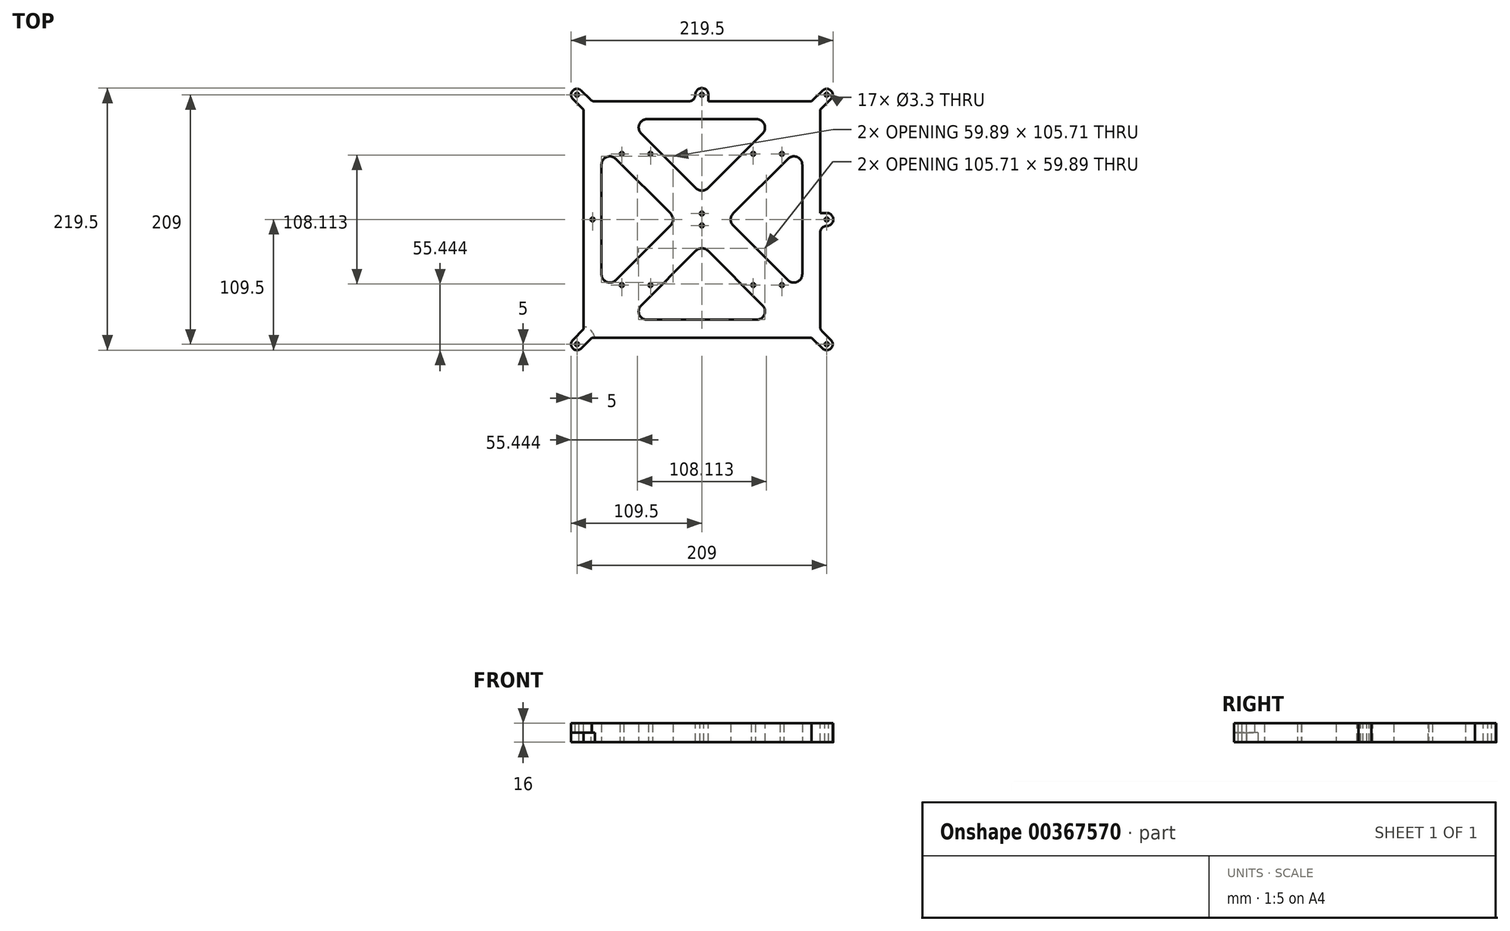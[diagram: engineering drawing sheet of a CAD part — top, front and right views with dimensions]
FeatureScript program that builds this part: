
annotation { "Feature Type Name" : "Feature", "Feature Type Description" : "" }
export const myFeature = defineFeature(function(context is Context, id is Id, definition is map)
    precondition{}
    {
        {
            var Q0;
            Q0=qCreatedBy(makeId("Top.planeOp"),FACE);
            var sketch = newSketch(context, id + "F0", { "sketchPlane" : qUnion([Q0])});
            skLineSegment(sketch, "E0.bottom", {"start": v(99, 99) * mm, "end": v(-99, 99) * mm});
            skLineSegment(sketch, "E0.top", {"start": v(99, -99) * mm, "end": v(-99, -99) * mm});
            skLineSegment(sketch, "E0.left", {"start": v(99, 99) * mm, "end": v(99, -99) * mm});
            skLineSegment(sketch, "E0.right", {"start": v(-99, 99) * mm, "end": v(-99, -99) * mm});
            skPoint(sketch, "E0.middle", {"position": v(0, 0) * mm});
            skLineSegment(sketch, "E1", {"start": v(99, 99) * mm, "end": v(-99, -99) * mm, "construction": true});
            skLineSegment(sketch, "E2", {"start": v(0, 21.21) * mm, "end": v(62.79, 84) * mm});
            skLineSegment(sketch, "E3.MirrorCS", {"start": v(0, 21.21) * mm, "end": v(-62.79, 84) * mm});
            skLineSegment(sketch, "E4", {"start": v(62.79, 84) * mm, "end": v(-62.79, 84) * mm});
            skLineSegment(sketch, "E5", {"start": v(-99, 99) * mm, "end": v(99, -99) * mm, "construction": true});
            skLineSegment(sketch, "E6.MirrorCS", {"start": v(-21.21, 0) * mm, "end": v(-84, 62.79) * mm});
            skLineSegment(sketch, "E7.MirrorCS", {"start": v(-84, -62.79) * mm, "end": v(-84, 62.79) * mm});
            skLineSegment(sketch, "E8.MirrorCS", {"start": v(-21.21, 0) * mm, "end": v(-84, -62.79) * mm});
            skLineSegment(sketch, "E9.MirrorCS", {"start": v(21.21, 0) * mm, "end": v(84, 62.79) * mm});
            skLineSegment(sketch, "E10.MirrorCS", {"start": v(84, 62.79) * mm, "end": v(84, -62.79) * mm});
            skLineSegment(sketch, "E11.MirrorCS", {"start": v(21.21, 0) * mm, "end": v(84, -62.79) * mm});
            skLineSegment(sketch, "E12.MirrorCS", {"start": v(0, -21.21) * mm, "end": v(-62.79, -84) * mm});
            skLineSegment(sketch, "E13.MirrorCS", {"start": v(0, -21.21) * mm, "end": v(62.79, -84) * mm});
            skLineSegment(sketch, "E14.MirrorCS", {"start": v(-62.79, -84) * mm, "end": v(62.79, -84) * mm});
            skLineSegment(sketch, "E15", {"start": v(-55, 55) * mm, "end": v(-43, 55) * mm, "construction": true});
            skLineSegment(sketch, "E16", {"start": v(-55, 55) * mm, "end": v(-67, 55) * mm, "construction": true});
            skLineSegment(sketch, "E17.MirrorCS", {"start": v(55, 55) * mm, "end": v(67, 55) * mm, "construction": true});
            skLineSegment(sketch, "E18.MirrorCS", {"start": v(55, 55) * mm, "end": v(43, 55) * mm, "construction": true});
            skLineSegment(sketch, "E19.MirrorCS", {"start": v(55, -55) * mm, "end": v(67, -55) * mm, "construction": true});
            skLineSegment(sketch, "E20.MirrorCS", {"start": v(-55, -55) * mm, "end": v(-43, -55) * mm, "construction": true});
            skLineSegment(sketch, "E21.MirrorCS", {"start": v(-55, -55) * mm, "end": v(-67, -55) * mm, "construction": true});
            skLineSegment(sketch, "E22.MirrorCS", {"start": v(55, -55) * mm, "end": v(43, -55) * mm, "construction": true});
            skSolve(sketch);
        }
        {
            var Q0;
            Q0=makeQuery(id+"F0.imprint","IMPRINT",FACE,{"disambiguationData":[TD([[makeQuery(id+"F0.imprint","IMPRINT",EDGE,{"derivedFrom":sQuery(id+"F0.wireOp",EDGE,"E0.bottom")}),1.0]])]});
            extrude(context, id + "F1", {"entities" : qUnion([Q0]), "depth" : 16 * mm});
        }
        {
            var Q0;
            Q0=makeQuery(id+"F1.opExtrude","CAP_FACE",FACE,{"disambiguationData":[OSD([sQuery(id+"F0.wireOp",EDGE,"E0.bottom"),sQuery(id+"F0.wireOp",EDGE,"E0.top"),sQuery(id+"F0.wireOp",EDGE,"E0.left"),sQuery(id+"F0.wireOp",EDGE,"E0.right"),sQuery(id+"F0.wireOp",EDGE,"E2"),sQuery(id+"F0.wireOp",EDGE,"E3.MirrorCS"),sQuery(id+"F0.wireOp",EDGE,"E4"),sQuery(id+"F0.wireOp",EDGE,"E6.MirrorCS"),sQuery(id+"F0.wireOp",EDGE,"E7.MirrorCS"),sQuery(id+"F0.wireOp",EDGE,"E8.MirrorCS"),sQuery(id+"F0.wireOp",EDGE,"E9.MirrorCS"),sQuery(id+"F0.wireOp",EDGE,"E10.MirrorCS"),sQuery(id+"F0.wireOp",EDGE,"E11.MirrorCS"),sQuery(id+"F0.wireOp",EDGE,"E12.MirrorCS"),sQuery(id+"F0.wireOp",EDGE,"E13.MirrorCS"),sQuery(id+"F0.wireOp",EDGE,"E14.MirrorCS")])],"isStart":false});
            var sketch = newSketch(context, id + "F2", { "sketchPlane" : qUnion([Q0])});
            skLineSegment(sketch, "E23", {"start": v(-99, 99) * mm, "end": v(-104.5, 104.5) * mm, "construction": true});
            skLineSegment(sketch, "E24.0", {"start": v(-91.93, 99) * mm, "end": v(-100.96, 108.04) * mm});
            skLineSegment(sketch, "E25.0", {"start": v(-99, 91.93) * mm, "end": v(-108.04, 100.96) * mm});
            skArc(sketch, "E26", {"start": v(-108.04, 100.96) * mm, "mid": v(-108.04, 108.04) * mm, "end": v(-100.96, 108.04) * mm});
            skLineSegment(sketch, "E27.MirrorCS", {"start": v(99, 91.93) * mm, "end": v(108.04, 100.96) * mm});
            skLineSegment(sketch, "E28.MirrorCS", {"start": v(99, 99) * mm, "end": v(104.5, 104.5) * mm, "construction": true});
            skLineSegment(sketch, "E29.MirrorCS", {"start": v(91.93, 99) * mm, "end": v(100.96, 108.04) * mm});
            skArc(sketch, "E30.MirrorCS", {"start": v(108.04, 100.96) * mm, "mid": v(108.04, 108.04) * mm, "end": v(100.96, 108.04) * mm});
            skLineSegment(sketch, "E31.MirrorCS", {"start": v(99, -99) * mm, "end": v(104.5, -104.5) * mm, "construction": true});
            skLineSegment(sketch, "E32.MirrorCS", {"start": v(-99, -99) * mm, "end": v(-104.5, -104.5) * mm, "construction": true});
            skLineSegment(sketch, "E33.MirrorCS", {"start": v(-99, -91.93) * mm, "end": v(-108.04, -100.96) * mm});
            skLineSegment(sketch, "E34.MirrorCS", {"start": v(91.93, -99) * mm, "end": v(100.96, -108.04) * mm});
            skArc(sketch, "E35.MirrorCS", {"start": v(108.04, -100.96) * mm, "mid": v(108.04, -108.04) * mm, "end": v(100.96, -108.04) * mm});
            skLineSegment(sketch, "E36.MirrorCS", {"start": v(99, -91.93) * mm, "end": v(108.04, -100.96) * mm});
            skArc(sketch, "E37.MirrorCS", {"start": v(-108.04, -100.96) * mm, "mid": v(-108.04, -108.04) * mm, "end": v(-100.96, -108.04) * mm});
            skLineSegment(sketch, "E38.MirrorCS", {"start": v(-91.93, -99) * mm, "end": v(-100.96, -108.04) * mm});
            skLineSegment(sketch, "E39", {"start": v(-5.5, 99) * mm, "end": v(-5.5, 110) * mm});
            skLineSegment(sketch, "E40", {"start": v(-5.5, 110) * mm, "end": v(5.5, 110) * mm});
            skLineSegment(sketch, "E41", {"start": v(5.5, 110) * mm, "end": v(5.5, 99) * mm});
            skLineSegment(sketch, "E42", {"start": v(99, 5.5) * mm, "end": v(110, 5.5) * mm});
            skLineSegment(sketch, "E43", {"start": v(110, 5.5) * mm, "end": v(110, -5.5) * mm});
            skLineSegment(sketch, "E44", {"start": v(110, -5.5) * mm, "end": v(99, -5.5) * mm});
            skLineSegment(sketch, "E45", {"start": v(110, 0) * mm, "end": v(99, 0) * mm, "construction": true});
            skLineSegment(sketch, "E46", {"start": v(0, 110) * mm, "end": v(0, 99) * mm, "construction": true});
            skLineSegment(sketch, "E47", {"start": v(0, 104.5) * mm, "end": v(5.5, 110) * mm, "construction": true});
            skLineSegment(sketch, "E48", {"start": v(104.5, 0) * mm, "end": v(110, -5.5) * mm, "construction": true});
            skLineSegment(sketch, "E49", {"start": v(0, 0) * mm, "end": v(0, -5) * mm, "construction": true});
            skLineSegment(sketch, "E50", {"start": v(0, 0) * mm, "end": v(0, 5) * mm, "construction": true});
            skSolve(sketch);
        }
        {
            var Q0;
            {var subQ4=sQuery(id+"F2.wireOp",EDGE,"E33.MirrorCS");Q0=makeQuery(id+"F2.imprint","IMPRINT",FACE,{"disambiguationData":[TD([[makeQuery(id+"F2.imprint","IMPRINT",EDGE,{"derivedFrom":subQ4}),1.0]])]});}
            var Q1;
            {var subQ3=sQuery(id+"F2.wireOp",EDGE,"E34.MirrorCS");Q1=makeQuery(id+"F2.imprint","IMPRINT",FACE,{"disambiguationData":[TD([[makeQuery(id+"F2.imprint","IMPRINT",EDGE,{"derivedFrom":subQ3}),1.0]])]});}
            var Q2;
            {var subQ0=sQuery(id+"F2.wireOp",EDGE,"E42");Q2=makeQuery(id+"F2.imprint","IMPRINT",FACE,{"disambiguationData":[TD([[makeQuery(id+"F2.imprint","IMPRINT",EDGE,{"derivedFrom":subQ0}),-1.0]])]});}
            var Q3;
            {var subQ4=sQuery(id+"F2.wireOp",EDGE,"E27.MirrorCS");Q3=makeQuery(id+"F2.imprint","IMPRINT",FACE,{"disambiguationData":[TD([[makeQuery(id+"F2.imprint","IMPRINT",EDGE,{"derivedFrom":subQ4}),1.0]])]});}
            var Q4;
            {var subQ3=sQuery(id+"F2.wireOp",EDGE,"E24.0");Q4=makeQuery(id+"F2.imprint","IMPRINT",FACE,{"disambiguationData":[TD([[makeQuery(id+"F2.imprint","IMPRINT",EDGE,{"derivedFrom":subQ3}),1.0]])]});}
            var Q5;
            {var subQ0=sQuery(id+"F2.wireOp",EDGE,"E39");Q5=makeQuery(id+"F2.imprint","IMPRINT",FACE,{"disambiguationData":[TD([[makeQuery(id+"F2.imprint","IMPRINT",EDGE,{"derivedFrom":subQ0}),-1.0]])]});}
            var Q6;
            Q6=makeQuery(id+"F1.opExtrude","CAP_FACE",FACE,{"disambiguationData":[OSD([sQuery(id+"F0.wireOp",EDGE,"E0.bottom"),sQuery(id+"F0.wireOp",EDGE,"E0.top"),sQuery(id+"F0.wireOp",EDGE,"E0.left"),sQuery(id+"F0.wireOp",EDGE,"E0.right"),sQuery(id+"F0.wireOp",EDGE,"E2"),sQuery(id+"F0.wireOp",EDGE,"E3.MirrorCS"),sQuery(id+"F0.wireOp",EDGE,"E4"),sQuery(id+"F0.wireOp",EDGE,"E6.MirrorCS"),sQuery(id+"F0.wireOp",EDGE,"E7.MirrorCS"),sQuery(id+"F0.wireOp",EDGE,"E8.MirrorCS"),sQuery(id+"F0.wireOp",EDGE,"E9.MirrorCS"),sQuery(id+"F0.wireOp",EDGE,"E10.MirrorCS"),sQuery(id+"F0.wireOp",EDGE,"E11.MirrorCS"),sQuery(id+"F0.wireOp",EDGE,"E12.MirrorCS"),sQuery(id+"F0.wireOp",EDGE,"E13.MirrorCS"),sQuery(id+"F0.wireOp",EDGE,"E14.MirrorCS")])],"isStart":true});
            extrude(context, id + "F3", {"entities" : qUnion([Q0, Q1, Q2, Q3, Q4, Q5]), "operationType" : NewBodyOperationType.ADD, "endBound" : BoundingType.UP_TO_SURFACE, "oppositeDirection" : true, "endBoundEntityFace" : qUnion([Q6]), "depth" : 25 * mm});
        }
        {
            var Q0;
            {var subQ0=sQuery(id+"F0.wireOp",EDGE,"E0.left");var subQ1=sQuery(id+"F0.wireOp",EDGE,"E14.MirrorCS");var subQ2=sQuery(id+"F0.wireOp",EDGE,"E13.MirrorCS");var subQ3=sQuery(id+"F0.wireOp",EDGE,"E12.MirrorCS");var subQ4=sQuery(id+"F0.wireOp",EDGE,"E11.MirrorCS");var subQ5=sQuery(id+"F0.wireOp",EDGE,"E10.MirrorCS");var subQ6=sQuery(id+"F0.wireOp",EDGE,"E9.MirrorCS");var subQ7=sQuery(id+"F0.wireOp",EDGE,"E8.MirrorCS");var subQ8=sQuery(id+"F0.wireOp",EDGE,"E7.MirrorCS");var subQ9=sQuery(id+"F0.wireOp",EDGE,"E6.MirrorCS");var subQ10=sQuery(id+"F0.wireOp",EDGE,"E4");var subQ11=sQuery(id+"F0.wireOp",EDGE,"E3.MirrorCS");var subQ12=sQuery(id+"F0.wireOp",EDGE,"E2");var subQ13=sQuery(id+"F0.wireOp",EDGE,"E0.right");var subQ14=sQuery(id+"F0.wireOp",EDGE,"E0.top");var subQ15=sQuery(id+"F0.wireOp",EDGE,"E0.bottom");Q0=makeQuery(id+"F3.boolean.opBoolean","MERGE",FACE,{"derivedFrom":[makeQuery(id+"F1.opExtrude","CAP_FACE",FACE,{"disambiguationData":[OSD([subQ15,subQ14,subQ0,subQ13,subQ12,subQ11,subQ10,subQ9,subQ8,subQ7,subQ6,subQ5,subQ4,subQ3,subQ2,subQ1])],"isStart":true}),makeQuery(id+"F3.opExtrude","CAP_FACE",FACE,{"disambiguationData":[OSD([subQ15,subQ14,subQ0,subQ13,subQ12,subQ11,subQ10,subQ9,subQ8,subQ7,subQ6,subQ5,subQ4,subQ3,subQ2,subQ1]),ownerDisambiguation([makeQuery(id+"F3.opExtrude","SWEPT_BODY",BODY,{"disambiguationData":[OSD([subQ15,subQ13,sQuery(id+"F2.wireOp",EDGE,"E24.0"),sQuery(id+"F2.wireOp",EDGE,"E25.0"),sQuery(id+"F2.wireOp",EDGE,"E26")])]})])],"isStart":false}),makeQuery(id+"F3.opExtrude","CAP_FACE",FACE,{"disambiguationData":[OSD([subQ15,subQ14,subQ0,subQ13,subQ12,subQ11,subQ10,subQ9,subQ8,subQ7,subQ6,subQ5,subQ4,subQ3,subQ2,subQ1]),ownerDisambiguation([makeQuery(id+"F3.opExtrude","SWEPT_BODY",BODY,{"disambiguationData":[OSD([subQ15,subQ0,sQuery(id+"F2.wireOp",EDGE,"E27.MirrorCS"),sQuery(id+"F2.wireOp",EDGE,"E29.MirrorCS"),sQuery(id+"F2.wireOp",EDGE,"E30.MirrorCS")])]})])],"isStart":false}),makeQuery(id+"F3.opExtrude","CAP_FACE",FACE,{"disambiguationData":[OSD([subQ15,subQ14,subQ0,subQ13,subQ12,subQ11,subQ10,subQ9,subQ8,subQ7,subQ6,subQ5,subQ4,subQ3,subQ2,subQ1]),ownerDisambiguation([makeQuery(id+"F3.opExtrude","SWEPT_BODY",BODY,{"disambiguationData":[OSD([subQ14,subQ13,sQuery(id+"F2.wireOp",EDGE,"E33.MirrorCS"),sQuery(id+"F2.wireOp",EDGE,"E37.MirrorCS"),sQuery(id+"F2.wireOp",EDGE,"E38.MirrorCS")])]})])],"isStart":false}),makeQuery(id+"F3.opExtrude","CAP_FACE",FACE,{"disambiguationData":[OSD([subQ15,subQ14,subQ0,subQ13,subQ12,subQ11,subQ10,subQ9,subQ8,subQ7,subQ6,subQ5,subQ4,subQ3,subQ2,subQ1]),ownerDisambiguation([makeQuery(id+"F3.opExtrude","SWEPT_BODY",BODY,{"disambiguationData":[OSD([subQ14,subQ0,sQuery(id+"F2.wireOp",EDGE,"E34.MirrorCS"),sQuery(id+"F2.wireOp",EDGE,"E35.MirrorCS"),sQuery(id+"F2.wireOp",EDGE,"E36.MirrorCS")])]})])],"isStart":false}),makeQuery(id+"F3.opExtrude","CAP_FACE",FACE,{"disambiguationData":[OSD([subQ15,subQ14,subQ0,subQ13,subQ12,subQ11,subQ10,subQ9,subQ8,subQ7,subQ6,subQ5,subQ4,subQ3,subQ2,subQ1]),ownerDisambiguation([makeQuery(id+"F3.opExtrude","SWEPT_BODY",BODY,{"disambiguationData":[OSD([subQ15,sQuery(id+"F2.wireOp",EDGE,"E39"),sQuery(id+"F2.wireOp",EDGE,"E40"),sQuery(id+"F2.wireOp",EDGE,"E41")])]})])],"isStart":false}),makeQuery(id+"F3.opExtrude","CAP_FACE",FACE,{"disambiguationData":[OSD([subQ15,subQ14,subQ0,subQ13,subQ12,subQ11,subQ10,subQ9,subQ8,subQ7,subQ6,subQ5,subQ4,subQ3,subQ2,subQ1]),ownerDisambiguation([makeQuery(id+"F3.opExtrude","SWEPT_BODY",BODY,{"disambiguationData":[OSD([subQ0,sQuery(id+"F2.wireOp",EDGE,"E42"),sQuery(id+"F2.wireOp",EDGE,"E43"),sQuery(id+"F2.wireOp",EDGE,"E44")])]})])],"isStart":false})]});}
            var sketch = newSketch(context, id + "F4", { "sketchPlane" : qUnion([Q0])});
            skPoint(sketch, "E51.0", {"position": v(-101.75, -101.75) * mm});
            skPoint(sketch, "E52.0", {"position": v(0, -104.5) * mm});
            skPoint(sketch, "E53.0", {"position": v(101.75, -101.75) * mm});
            skPoint(sketch, "E54.0", {"position": v(104.5, 0) * mm});
            skPoint(sketch, "E55.0", {"position": v(101.75, 101.75) * mm});
            skPoint(sketch, "E56.0", {"position": v(-101.75, 101.75) * mm});
            skCircle(sketch, "E57", {"center": v(-101.75, 101.75) * mm, "radius": 12.5 * mm});
            skCircle(sketch, "E58", {"center": v(101.75, 101.75) * mm, "radius": 12.5 * mm});
            skCircle(sketch, "E59", {"center": v(-101.75, -101.75) * mm, "radius": 12.5 * mm});
            skCircle(sketch, "E60", {"center": v(101.75, -101.75) * mm, "radius": 12.5 * mm});
            skCircle(sketch, "E61", {"center": v(0, -104.5) * mm, "radius": 10 * mm});
            skCircle(sketch, "E62", {"center": v(104.5, 0) * mm, "radius": 10 * mm});
            skLineSegment(sketch, "E63", {"start": v(-99, 0) * mm, "end": v(-84, 0) * mm});
            skCircle(sketch, "E64", {"center": v(-91.5, 0) * mm, "radius": 2.5 * mm});
            skSolve(sketch);
        }
        {
            var Q0;
            {var subQ1=sQuery(id+"F0.wireOp",EDGE,"E0.top");var subQ6=sQuery(id+"F4.wireOp",EDGE,"E57");var subQ8=makeQuery(id+"F1.opExtrude","CAP_EDGE",EDGE,{"disambiguationData":[OSD([subQ1])],"isStart":true});var subQ9=makeQuery(id+"F4.imprint","INTERSECT",VERTEX,{"derivedFrom":[subQ8,subQ6]});Q0=makeQuery(id+"F4.imprint","IMPRINT",FACE,{"disambiguationData":[TD([[makeQuery(id+"F4.imprint","IMPRINT",EDGE,{"disambiguationData":[TD([[subQ9,1.0]])],"derivedFrom":subQ6}),1.0]])]});}
            var Q1;
            {var subQ1=sQuery(id+"F0.wireOp",EDGE,"E14.MirrorCS");var subQ2=sQuery(id+"F0.wireOp",EDGE,"E13.MirrorCS");var subQ3=sQuery(id+"F0.wireOp",EDGE,"E12.MirrorCS");var subQ4=sQuery(id+"F0.wireOp",EDGE,"E11.MirrorCS");var subQ5=sQuery(id+"F0.wireOp",EDGE,"E10.MirrorCS");var subQ6=sQuery(id+"F0.wireOp",EDGE,"E9.MirrorCS");var subQ7=sQuery(id+"F0.wireOp",EDGE,"E8.MirrorCS");var subQ8=sQuery(id+"F0.wireOp",EDGE,"E7.MirrorCS");var subQ9=sQuery(id+"F0.wireOp",EDGE,"E6.MirrorCS");var subQ10=sQuery(id+"F0.wireOp",EDGE,"E4");var subQ11=sQuery(id+"F0.wireOp",EDGE,"E3.MirrorCS");var subQ12=sQuery(id+"F0.wireOp",EDGE,"E2");var subQ13=sQuery(id+"F0.wireOp",EDGE,"E0.right");var subQ14=sQuery(id+"F0.wireOp",EDGE,"E0.left");var subQ15=sQuery(id+"F0.wireOp",EDGE,"E0.top");var subQ16=sQuery(id+"F0.wireOp",EDGE,"E0.bottom");var subQ17=makeQuery(id+"F1.opExtrude","CAP_FACE",FACE,{"disambiguationData":[OSD([subQ16,subQ15,subQ14,subQ13,subQ12,subQ11,subQ10,subQ9,subQ8,subQ7,subQ6,subQ5,subQ4,subQ3,subQ2,subQ1])],"isStart":true});var subQ22=sQuery(id+"F2.wireOp",EDGE,"E24.0");var subQ26=makeQuery(id+"F3.opExtrude","TWEAK_EDGE",EDGE,{"derivedFrom":[subQ17,makeQuery(id+"F2.imprint","IMPRINT",EDGE,{"derivedFrom":subQ22})]});Q1=makeQuery(id+"F4.imprint","IMPRINT",FACE,{"disambiguationData":[TD([[makeQuery(id+"F4.imprint","IMPRINT",EDGE,{"derivedFrom":subQ26}),1.0]])]});}
            var Q2;
            {var subQ1=sQuery(id+"F0.wireOp",EDGE,"E14.MirrorCS");var subQ2=sQuery(id+"F0.wireOp",EDGE,"E13.MirrorCS");var subQ3=sQuery(id+"F0.wireOp",EDGE,"E12.MirrorCS");var subQ4=sQuery(id+"F0.wireOp",EDGE,"E11.MirrorCS");var subQ5=sQuery(id+"F0.wireOp",EDGE,"E10.MirrorCS");var subQ6=sQuery(id+"F0.wireOp",EDGE,"E9.MirrorCS");var subQ7=sQuery(id+"F0.wireOp",EDGE,"E8.MirrorCS");var subQ8=sQuery(id+"F0.wireOp",EDGE,"E7.MirrorCS");var subQ9=sQuery(id+"F0.wireOp",EDGE,"E6.MirrorCS");var subQ10=sQuery(id+"F0.wireOp",EDGE,"E4");var subQ11=sQuery(id+"F0.wireOp",EDGE,"E3.MirrorCS");var subQ12=sQuery(id+"F0.wireOp",EDGE,"E2");var subQ13=sQuery(id+"F0.wireOp",EDGE,"E0.right");var subQ14=sQuery(id+"F0.wireOp",EDGE,"E0.left");var subQ15=sQuery(id+"F0.wireOp",EDGE,"E0.top");var subQ16=sQuery(id+"F0.wireOp",EDGE,"E0.bottom");var subQ17=makeQuery(id+"F1.opExtrude","CAP_FACE",FACE,{"disambiguationData":[OSD([subQ16,subQ15,subQ14,subQ13,subQ12,subQ11,subQ10,subQ9,subQ8,subQ7,subQ6,subQ5,subQ4,subQ3,subQ2,subQ1])],"isStart":true});var subQ18=sQuery(id+"F2.wireOp",EDGE,"E39");var subQ19=makeQuery(id+"F3.opExtrude","TWEAK_EDGE",EDGE,{"derivedFrom":[subQ17,makeQuery(id+"F2.imprint","IMPRINT",EDGE,{"derivedFrom":subQ18})]});Q2=makeQuery(id+"F4.imprint","IMPRINT",FACE,{"disambiguationData":[TD([[makeQuery(id+"F4.imprint","IMPRINT",EDGE,{"derivedFrom":subQ19}),-1.0]])]});}
            var Q3;
            {var subQ1=sQuery(id+"F0.wireOp",EDGE,"E14.MirrorCS");var subQ2=sQuery(id+"F0.wireOp",EDGE,"E13.MirrorCS");var subQ3=sQuery(id+"F0.wireOp",EDGE,"E12.MirrorCS");var subQ4=sQuery(id+"F0.wireOp",EDGE,"E11.MirrorCS");var subQ5=sQuery(id+"F0.wireOp",EDGE,"E10.MirrorCS");var subQ6=sQuery(id+"F0.wireOp",EDGE,"E9.MirrorCS");var subQ7=sQuery(id+"F0.wireOp",EDGE,"E8.MirrorCS");var subQ8=sQuery(id+"F0.wireOp",EDGE,"E7.MirrorCS");var subQ9=sQuery(id+"F0.wireOp",EDGE,"E6.MirrorCS");var subQ10=sQuery(id+"F0.wireOp",EDGE,"E4");var subQ11=sQuery(id+"F0.wireOp",EDGE,"E3.MirrorCS");var subQ12=sQuery(id+"F0.wireOp",EDGE,"E2");var subQ13=sQuery(id+"F0.wireOp",EDGE,"E0.right");var subQ14=sQuery(id+"F0.wireOp",EDGE,"E0.left");var subQ15=sQuery(id+"F0.wireOp",EDGE,"E0.top");var subQ16=sQuery(id+"F0.wireOp",EDGE,"E0.bottom");var subQ17=makeQuery(id+"F1.opExtrude","CAP_FACE",FACE,{"disambiguationData":[OSD([subQ16,subQ15,subQ14,subQ13,subQ12,subQ11,subQ10,subQ9,subQ8,subQ7,subQ6,subQ5,subQ4,subQ3,subQ2,subQ1])],"isStart":true});var subQ19=sQuery(id+"F2.wireOp",EDGE,"E42");var subQ20=makeQuery(id+"F3.opExtrude","TWEAK_EDGE",EDGE,{"derivedFrom":[subQ17,makeQuery(id+"F2.imprint","IMPRINT",EDGE,{"derivedFrom":subQ19})]});Q3=makeQuery(id+"F4.imprint","IMPRINT",FACE,{"disambiguationData":[TD([[makeQuery(id+"F4.imprint","IMPRINT",EDGE,{"derivedFrom":subQ20}),-1.0]])]});}
            var Q4;
            {var subQ1=sQuery(id+"F0.wireOp",EDGE,"E14.MirrorCS");var subQ2=sQuery(id+"F0.wireOp",EDGE,"E13.MirrorCS");var subQ3=sQuery(id+"F0.wireOp",EDGE,"E12.MirrorCS");var subQ4=sQuery(id+"F0.wireOp",EDGE,"E11.MirrorCS");var subQ5=sQuery(id+"F0.wireOp",EDGE,"E10.MirrorCS");var subQ6=sQuery(id+"F0.wireOp",EDGE,"E9.MirrorCS");var subQ7=sQuery(id+"F0.wireOp",EDGE,"E8.MirrorCS");var subQ8=sQuery(id+"F0.wireOp",EDGE,"E7.MirrorCS");var subQ9=sQuery(id+"F0.wireOp",EDGE,"E6.MirrorCS");var subQ10=sQuery(id+"F0.wireOp",EDGE,"E4");var subQ11=sQuery(id+"F0.wireOp",EDGE,"E3.MirrorCS");var subQ12=sQuery(id+"F0.wireOp",EDGE,"E2");var subQ13=sQuery(id+"F0.wireOp",EDGE,"E0.right");var subQ14=sQuery(id+"F0.wireOp",EDGE,"E0.left");var subQ15=sQuery(id+"F0.wireOp",EDGE,"E0.top");var subQ16=sQuery(id+"F0.wireOp",EDGE,"E0.bottom");var subQ17=makeQuery(id+"F1.opExtrude","CAP_FACE",FACE,{"disambiguationData":[OSD([subQ16,subQ15,subQ14,subQ13,subQ12,subQ11,subQ10,subQ9,subQ8,subQ7,subQ6,subQ5,subQ4,subQ3,subQ2,subQ1])],"isStart":true});var subQ19=sQuery(id+"F2.wireOp",EDGE,"E34.MirrorCS");var subQ20=makeQuery(id+"F3.opExtrude","TWEAK_EDGE",EDGE,{"derivedFrom":[subQ17,makeQuery(id+"F2.imprint","IMPRINT",EDGE,{"derivedFrom":subQ19})]});Q4=makeQuery(id+"F4.imprint","IMPRINT",FACE,{"disambiguationData":[TD([[makeQuery(id+"F4.imprint","IMPRINT",EDGE,{"derivedFrom":subQ20}),1.0]])]});}
            var Q5;
            {var subQ1=sQuery(id+"F0.wireOp",EDGE,"E14.MirrorCS");var subQ2=sQuery(id+"F0.wireOp",EDGE,"E13.MirrorCS");var subQ3=sQuery(id+"F0.wireOp",EDGE,"E12.MirrorCS");var subQ4=sQuery(id+"F0.wireOp",EDGE,"E11.MirrorCS");var subQ5=sQuery(id+"F0.wireOp",EDGE,"E10.MirrorCS");var subQ6=sQuery(id+"F0.wireOp",EDGE,"E9.MirrorCS");var subQ7=sQuery(id+"F0.wireOp",EDGE,"E8.MirrorCS");var subQ8=sQuery(id+"F0.wireOp",EDGE,"E7.MirrorCS");var subQ9=sQuery(id+"F0.wireOp",EDGE,"E6.MirrorCS");var subQ10=sQuery(id+"F0.wireOp",EDGE,"E4");var subQ11=sQuery(id+"F0.wireOp",EDGE,"E3.MirrorCS");var subQ12=sQuery(id+"F0.wireOp",EDGE,"E2");var subQ13=sQuery(id+"F0.wireOp",EDGE,"E0.right");var subQ14=sQuery(id+"F0.wireOp",EDGE,"E0.left");var subQ15=sQuery(id+"F0.wireOp",EDGE,"E0.top");var subQ16=sQuery(id+"F0.wireOp",EDGE,"E0.bottom");var subQ17=makeQuery(id+"F1.opExtrude","CAP_FACE",FACE,{"disambiguationData":[OSD([subQ16,subQ15,subQ14,subQ13,subQ12,subQ11,subQ10,subQ9,subQ8,subQ7,subQ6,subQ5,subQ4,subQ3,subQ2,subQ1])],"isStart":true});var subQ23=sQuery(id+"F2.wireOp",EDGE,"E27.MirrorCS");var subQ34=makeQuery(id+"F3.opExtrude","TWEAK_EDGE",EDGE,{"derivedFrom":[subQ17,makeQuery(id+"F2.imprint","IMPRINT",EDGE,{"derivedFrom":subQ23})]});Q5=makeQuery(id+"F4.imprint","IMPRINT",FACE,{"disambiguationData":[TD([[makeQuery(id+"F4.imprint","IMPRINT",EDGE,{"derivedFrom":subQ34}),1.0]])]});}
            extrude(context, id + "F5", {"entities" : qUnion([Q0, Q1, Q2, Q3, Q4, Q5]), "operationType" : NewBodyOperationType.REMOVE, "oppositeDirection" : true, "depth" : 8 * mm});
        }
        {
            var Q0;
            Q0=makeQuery(id+"F3.opExtrude","SWEPT_EDGE",EDGE,{"disambiguationData":[OSD([sQuery(id+"F0.wireOp",EDGE,"E0.bottom"),sQuery(id+"F2.wireOp",EDGE,"E24.0")])]});
            var Q1;
            Q1=makeQuery(id+"F3.opExtrude","SWEPT_EDGE",EDGE,{"disambiguationData":[OSD([sQuery(id+"F0.wireOp",EDGE,"E0.right"),sQuery(id+"F2.wireOp",EDGE,"E25.0")])]});
            var Q2;
            Q2=makeQuery(id+"F3.opExtrude","SWEPT_EDGE",EDGE,{"disambiguationData":[OSD([sQuery(id+"F0.wireOp",EDGE,"E0.right"),sQuery(id+"F2.wireOp",EDGE,"E33.MirrorCS")])]});
            var Q3;
            Q3=makeQuery(id+"F3.opExtrude","SWEPT_EDGE",EDGE,{"disambiguationData":[OSD([sQuery(id+"F0.wireOp",EDGE,"E0.top"),sQuery(id+"F2.wireOp",EDGE,"E38.MirrorCS")])]});
            var Q4;
            Q4=makeQuery(id+"F3.opExtrude","SWEPT_EDGE",EDGE,{"disambiguationData":[OSD([sQuery(id+"F0.wireOp",EDGE,"E0.top"),sQuery(id+"F2.wireOp",EDGE,"E34.MirrorCS")])]});
            var Q5;
            Q5=makeQuery(id+"F3.opExtrude","SWEPT_EDGE",EDGE,{"disambiguationData":[OSD([sQuery(id+"F0.wireOp",EDGE,"E0.left"),sQuery(id+"F2.wireOp",EDGE,"E36.MirrorCS")])]});
            var Q6;
            Q6=makeQuery(id+"F3.opExtrude","SWEPT_EDGE",EDGE,{"disambiguationData":[OSD([sQuery(id+"F0.wireOp",EDGE,"E0.left"),sQuery(id+"F2.wireOp",EDGE,"E27.MirrorCS")])]});
            var Q7;
            Q7=makeQuery(id+"F3.opExtrude","SWEPT_EDGE",EDGE,{"disambiguationData":[OSD([sQuery(id+"F0.wireOp",EDGE,"E0.bottom"),sQuery(id+"F2.wireOp",EDGE,"E29.MirrorCS")])]});
            var Q8;
            Q8=makeQuery(id+"F5.boolean.opBoolean","COPY",EDGE,{"derivedFrom":makeQuery(id+"F5.opExtrude","SWEPT_EDGE",EDGE,{"disambiguationData":[OSD([sQuery(id+"F0.wireOp",EDGE,"E0.bottom"),sQuery(id+"F4.wireOp",EDGE,"E60")])]})});
            var Q9;
            Q9=makeQuery(id+"F5.boolean.opBoolean","COPY",EDGE,{"derivedFrom":makeQuery(id+"F5.opExtrude","SWEPT_EDGE",EDGE,{"disambiguationData":[OSD([sQuery(id+"F0.wireOp",EDGE,"E0.left"),sQuery(id+"F4.wireOp",EDGE,"E60")])]})});
            var Q10;
            Q10=makeQuery(id+"F5.boolean.opBoolean","COPY",EDGE,{"derivedFrom":makeQuery(id+"F5.opExtrude","SWEPT_EDGE",EDGE,{"disambiguationData":[OSD([sQuery(id+"F0.wireOp",EDGE,"E0.left"),sQuery(id+"F4.wireOp",EDGE,"E58")])]})});
            var Q11;
            Q11=makeQuery(id+"F5.boolean.opBoolean","COPY",EDGE,{"derivedFrom":makeQuery(id+"F5.opExtrude","SWEPT_EDGE",EDGE,{"disambiguationData":[OSD([sQuery(id+"F0.wireOp",EDGE,"E0.top"),sQuery(id+"F4.wireOp",EDGE,"E58")])]})});
            var Q12;
            Q12=makeQuery(id+"F5.boolean.opBoolean","COPY",EDGE,{"derivedFrom":makeQuery(id+"F5.opExtrude","SWEPT_EDGE",EDGE,{"disambiguationData":[OSD([sQuery(id+"F0.wireOp",EDGE,"E0.top"),sQuery(id+"F4.wireOp",EDGE,"E57")])]})});
            var Q13;
            Q13=makeQuery(id+"F5.boolean.opBoolean","COPY",EDGE,{"derivedFrom":makeQuery(id+"F5.opExtrude","SWEPT_EDGE",EDGE,{"disambiguationData":[OSD([sQuery(id+"F0.wireOp",EDGE,"E0.right"),sQuery(id+"F4.wireOp",EDGE,"E57")])]})});
            var Q14;
            Q14=makeQuery(id+"F5.boolean.opBoolean","COPY",EDGE,{"derivedFrom":makeQuery(id+"F5.opExtrude","SWEPT_EDGE",EDGE,{"disambiguationData":[OSD([sQuery(id+"F0.wireOp",EDGE,"E0.bottom"),sQuery(id+"F4.wireOp",EDGE,"E59")])]})});
            var Q15;
            Q15=makeQuery(id+"F5.boolean.opBoolean","COPY",EDGE,{"derivedFrom":makeQuery(id+"F5.opExtrude","SWEPT_EDGE",EDGE,{"disambiguationData":[OSD([sQuery(id+"F0.wireOp",EDGE,"E0.right"),sQuery(id+"F4.wireOp",EDGE,"E59")])]})});
            fillet(context, id + "F6", {"entities" : qUnion([Q0, Q1, Q2, Q3, Q4, Q5, Q6, Q7, Q8, Q9, Q10, Q11, Q12, Q13, Q14, Q15]), "radius" : 5 * mm, "tangentPropagation" : true, "allowEdgeOverflow" : false});
        }
        {
            var Q0;
            Q0=makeQuery(id+"F1.opExtrude","SWEPT_EDGE",EDGE,{"disambiguationData":[OSD([sQuery(id+"F0.wireOp",EDGE,"E7.MirrorCS"),sQuery(id+"F0.wireOp",EDGE,"E8.MirrorCS")])]});
            var Q1;
            Q1=makeQuery(id+"F1.opExtrude","SWEPT_EDGE",EDGE,{"disambiguationData":[OSD([sQuery(id+"F0.wireOp",EDGE,"E6.MirrorCS"),sQuery(id+"F0.wireOp",EDGE,"E7.MirrorCS")])]});
            var Q2;
            Q2=makeQuery(id+"F1.opExtrude","SWEPT_EDGE",EDGE,{"disambiguationData":[OSD([sQuery(id+"F0.wireOp",EDGE,"E6.MirrorCS"),sQuery(id+"F0.wireOp",EDGE,"E8.MirrorCS")])]});
            var Q3;
            Q3=makeQuery(id+"F1.opExtrude","SWEPT_EDGE",EDGE,{"disambiguationData":[OSD([sQuery(id+"F0.wireOp",EDGE,"E13.MirrorCS"),sQuery(id+"F0.wireOp",EDGE,"E14.MirrorCS")])]});
            var Q4;
            Q4=makeQuery(id+"F1.opExtrude","SWEPT_EDGE",EDGE,{"disambiguationData":[OSD([sQuery(id+"F0.wireOp",EDGE,"E12.MirrorCS"),sQuery(id+"F0.wireOp",EDGE,"E14.MirrorCS")])]});
            var Q5;
            Q5=makeQuery(id+"F1.opExtrude","SWEPT_EDGE",EDGE,{"disambiguationData":[OSD([sQuery(id+"F0.wireOp",EDGE,"E12.MirrorCS"),sQuery(id+"F0.wireOp",EDGE,"E13.MirrorCS")])]});
            var Q6;
            Q6=makeQuery(id+"F1.opExtrude","SWEPT_EDGE",EDGE,{"disambiguationData":[OSD([sQuery(id+"F0.wireOp",EDGE,"E9.MirrorCS"),sQuery(id+"F0.wireOp",EDGE,"E11.MirrorCS")])]});
            var Q7;
            Q7=makeQuery(id+"F1.opExtrude","SWEPT_EDGE",EDGE,{"disambiguationData":[OSD([sQuery(id+"F0.wireOp",EDGE,"E10.MirrorCS"),sQuery(id+"F0.wireOp",EDGE,"E11.MirrorCS")])]});
            var Q8;
            Q8=makeQuery(id+"F1.opExtrude","SWEPT_EDGE",EDGE,{"disambiguationData":[OSD([sQuery(id+"F0.wireOp",EDGE,"E9.MirrorCS"),sQuery(id+"F0.wireOp",EDGE,"E10.MirrorCS")])]});
            var Q9;
            Q9=makeQuery(id+"F1.opExtrude","SWEPT_EDGE",EDGE,{"disambiguationData":[OSD([sQuery(id+"F0.wireOp",EDGE,"E2"),sQuery(id+"F0.wireOp",EDGE,"E4")])]});
            var Q10;
            Q10=makeQuery(id+"F1.opExtrude","SWEPT_EDGE",EDGE,{"disambiguationData":[OSD([sQuery(id+"F0.wireOp",EDGE,"E2"),sQuery(id+"F0.wireOp",EDGE,"E3.MirrorCS")])]});
            var Q11;
            Q11=makeQuery(id+"F1.opExtrude","SWEPT_EDGE",EDGE,{"disambiguationData":[OSD([sQuery(id+"F0.wireOp",EDGE,"E3.MirrorCS"),sQuery(id+"F0.wireOp",EDGE,"E4")])]});
            fillet(context, id + "F7", {"entities" : qUnion([Q0, Q1, Q2, Q3, Q4, Q5, Q6, Q7, Q8, Q9, Q10, Q11]), "radius" : 7 * mm, "tangentPropagation" : true, "allowEdgeOverflow" : false});
        }
        {
            var Q0;
            Q0=makeQuery(id+"F3.opExtrude","SWEPT_EDGE",EDGE,{"disambiguationData":[OSD([sQuery(id+"F0.wireOp",EDGE,"E0.left"),sQuery(id+"F2.wireOp",EDGE,"E44")])]});
            var Q1;
            Q1=makeQuery(id+"F3.opExtrude","SWEPT_EDGE",EDGE,{"disambiguationData":[OSD([sQuery(id+"F2.wireOp",EDGE,"E43"),sQuery(id+"F2.wireOp",EDGE,"E44")])]});
            var Q2;
            Q2=makeQuery(id+"F3.opExtrude","SWEPT_EDGE",EDGE,{"disambiguationData":[OSD([sQuery(id+"F2.wireOp",EDGE,"E42"),sQuery(id+"F2.wireOp",EDGE,"E43")])]});
            var Q3;
            Q3=makeQuery(id+"F3.opExtrude","SWEPT_EDGE",EDGE,{"disambiguationData":[OSD([sQuery(id+"F0.wireOp",EDGE,"E0.left"),sQuery(id+"F2.wireOp",EDGE,"E42")])]});
            var Q4;
            Q4=makeQuery(id+"F3.opExtrude","SWEPT_EDGE",EDGE,{"disambiguationData":[OSD([sQuery(id+"F2.wireOp",EDGE,"E39"),sQuery(id+"F2.wireOp",EDGE,"E40")])]});
            var Q5;
            Q5=makeQuery(id+"F3.opExtrude","SWEPT_EDGE",EDGE,{"disambiguationData":[OSD([sQuery(id+"F2.wireOp",EDGE,"E40"),sQuery(id+"F2.wireOp",EDGE,"E41")])]});
            var Q6;
            Q6=makeQuery(id+"F3.opExtrude","SWEPT_EDGE",EDGE,{"disambiguationData":[OSD([sQuery(id+"F0.wireOp",EDGE,"E0.bottom"),sQuery(id+"F2.wireOp",EDGE,"E39")])]});
            var Q7;
            Q7=makeQuery(id+"F3.opExtrude","SWEPT_EDGE",EDGE,{"disambiguationData":[OSD([sQuery(id+"F0.wireOp",EDGE,"E0.bottom"),sQuery(id+"F2.wireOp",EDGE,"E41")])]});
            fillet(context, id + "F8", {"entities" : qUnion([Q0, Q1, Q2, Q3, Q4, Q5, Q6, Q7]), "radius" : 5.5 * mm, "tangentPropagation" : true, "allowEdgeOverflow" : false});
        }
        {
            var Q0;
            Q0=sQuery(id+"F2.wireOp",VERTEX,"E28.MirrorCS.end");
            var Q1;
            Q1=sQuery(id+"F2.wireOp",VERTEX,"E23.end");
            var Q2;
            Q2=sQuery(id+"F2.wireOp",VERTEX,"E37.MirrorCS.center");
            var Q3;
            Q3=sQuery(id+"F2.wireOp",VERTEX,"E31.MirrorCS.end");
            var Q4;
            Q4=sQuery(id+"F2.wireOp",VERTEX,"E49.end");
            var Q5;
            Q5=sQuery(id+"F2.wireOp",VERTEX,"E50.end");
            var Q6;
            Q6=sQuery(id+"F2.wireOp",VERTEX,"E47.start");
            var Q7;
            Q7=sQuery(id+"F2.wireOp",VERTEX,"E48.start");
            var Q8;
            Q8=makeQuery(id+"F1.opExtrude","SWEPT_BODY",BODY,{"disambiguationData":[OSD([sQuery(id+"F0.wireOp",EDGE,"E0.bottom"),sQuery(id+"F0.wireOp",EDGE,"E0.top"),sQuery(id+"F0.wireOp",EDGE,"E0.left"),sQuery(id+"F0.wireOp",EDGE,"E0.right"),sQuery(id+"F0.wireOp",EDGE,"E2"),sQuery(id+"F0.wireOp",EDGE,"E3.MirrorCS"),sQuery(id+"F0.wireOp",EDGE,"E4"),sQuery(id+"F0.wireOp",EDGE,"E6.MirrorCS"),sQuery(id+"F0.wireOp",EDGE,"E7.MirrorCS"),sQuery(id+"F0.wireOp",EDGE,"E8.MirrorCS"),sQuery(id+"F0.wireOp",EDGE,"E9.MirrorCS"),sQuery(id+"F0.wireOp",EDGE,"E10.MirrorCS"),sQuery(id+"F0.wireOp",EDGE,"E11.MirrorCS"),sQuery(id+"F0.wireOp",EDGE,"E12.MirrorCS"),sQuery(id+"F0.wireOp",EDGE,"E13.MirrorCS"),sQuery(id+"F0.wireOp",EDGE,"E14.MirrorCS")])]});
            hole(context, id + "F9", {"style" : HoleStyle.SIMPLE, "endStyle" : HoleEndStyle.THROUGH, "standardTappedOrClearance" : lookupTablePath({ "standard" : "ISO", "fit" : "Normal", "size" : "M3", "type" : "Clearance" }), "standardBlindInLast" : lookupTablePath({ "fit" : "Standard", "standard" : "ISO", "size" : "M3", "type" : "Clearance" }), "holeDiameter" : 3.3 * mm, "tappedDepth" : 12 * mm, "tapClearance" : 3, "locations" : qUnion([Q0, Q1, Q2, Q3, Q4, Q5, Q6, Q7]), "scope" : qUnion([Q8])});
        }
        {
            var Q0;
            Q0=sQuery(id+"F0.wireOp",VERTEX,"E19.MirrorCS.end");
            var Q1;
            Q1=sQuery(id+"F0.wireOp",VERTEX,"E22.MirrorCS.end");
            var Q2;
            Q2=sQuery(id+"F0.wireOp",VERTEX,"E20.MirrorCS.end");
            var Q3;
            Q3=sQuery(id+"F0.wireOp",VERTEX,"E21.MirrorCS.end");
            var Q4;
            Q4=sQuery(id+"F0.wireOp",VERTEX,"E16.end");
            var Q5;
            Q5=sQuery(id+"F0.wireOp",VERTEX,"E15.end");
            var Q6;
            Q6=sQuery(id+"F0.wireOp",VERTEX,"E18.MirrorCS.end");
            var Q7;
            Q7=sQuery(id+"F0.wireOp",VERTEX,"E17.MirrorCS.end");
            var Q8;
            Q8=makeQuery(id+"F1.opExtrude","SWEPT_BODY",BODY,{"disambiguationData":[OSD([sQuery(id+"F0.wireOp",EDGE,"E0.bottom"),sQuery(id+"F0.wireOp",EDGE,"E0.top"),sQuery(id+"F0.wireOp",EDGE,"E0.left"),sQuery(id+"F0.wireOp",EDGE,"E0.right"),sQuery(id+"F0.wireOp",EDGE,"E2"),sQuery(id+"F0.wireOp",EDGE,"E3.MirrorCS"),sQuery(id+"F0.wireOp",EDGE,"E4"),sQuery(id+"F0.wireOp",EDGE,"E6.MirrorCS"),sQuery(id+"F0.wireOp",EDGE,"E7.MirrorCS"),sQuery(id+"F0.wireOp",EDGE,"E8.MirrorCS"),sQuery(id+"F0.wireOp",EDGE,"E9.MirrorCS"),sQuery(id+"F0.wireOp",EDGE,"E10.MirrorCS"),sQuery(id+"F0.wireOp",EDGE,"E11.MirrorCS"),sQuery(id+"F0.wireOp",EDGE,"E12.MirrorCS"),sQuery(id+"F0.wireOp",EDGE,"E13.MirrorCS"),sQuery(id+"F0.wireOp",EDGE,"E14.MirrorCS")])]});
            hole(context, id + "F10", {"style" : HoleStyle.SIMPLE, "endStyle" : HoleEndStyle.THROUGH, "oppositeDirection" : true, "standardTappedOrClearance" : lookupTablePath({ "standard" : "ISO", "fit" : "Normal", "size" : "M3", "type" : "Clearance" }), "standardBlindInLast" : lookupTablePath({ "fit" : "Standard", "standard" : "ISO", "size" : "M3", "type" : "Clearance" }), "holeDiameter" : 3.3 * mm, "tappedDepth" : 12 * mm, "tapClearance" : 3, "locations" : qUnion([Q0, Q1, Q2, Q3, Q4, Q5, Q6, Q7]), "scope" : qUnion([Q8])});
        }
        {
            var Q0;
            Q0=sQuery(id+"F4.wireOp",VERTEX,"E64.center");
            var Q1;
            Q1=makeQuery(id+"F1.opExtrude","SWEPT_BODY",BODY,{"disambiguationData":[OSD([sQuery(id+"F0.wireOp",EDGE,"E0.bottom"),sQuery(id+"F0.wireOp",EDGE,"E0.top"),sQuery(id+"F0.wireOp",EDGE,"E0.left"),sQuery(id+"F0.wireOp",EDGE,"E0.right"),sQuery(id+"F0.wireOp",EDGE,"E2"),sQuery(id+"F0.wireOp",EDGE,"E3.MirrorCS"),sQuery(id+"F0.wireOp",EDGE,"E4"),sQuery(id+"F0.wireOp",EDGE,"E6.MirrorCS"),sQuery(id+"F0.wireOp",EDGE,"E7.MirrorCS"),sQuery(id+"F0.wireOp",EDGE,"E8.MirrorCS"),sQuery(id+"F0.wireOp",EDGE,"E9.MirrorCS"),sQuery(id+"F0.wireOp",EDGE,"E10.MirrorCS"),sQuery(id+"F0.wireOp",EDGE,"E11.MirrorCS"),sQuery(id+"F0.wireOp",EDGE,"E12.MirrorCS"),sQuery(id+"F0.wireOp",EDGE,"E13.MirrorCS"),sQuery(id+"F0.wireOp",EDGE,"E14.MirrorCS")])]});
            hole(context, id + "F11", {"style" : HoleStyle.SIMPLE, "endStyle" : HoleEndStyle.THROUGH, "standardTappedOrClearance" : lookupTablePath({ "standard" : "ISO", "fit" : "Normal", "size" : "M3", "type" : "Clearance" }), "standardBlindInLast" : lookupTablePath({ "fit" : "Standard", "standard" : "ISO", "size" : "M3", "type" : "Clearance" }), "holeDiameter" : 3.3 * mm, "tappedDepth" : 12 * mm, "tapClearance" : 3, "locations" : qUnion([Q0]), "scope" : qUnion([Q1])});
        }
    });
